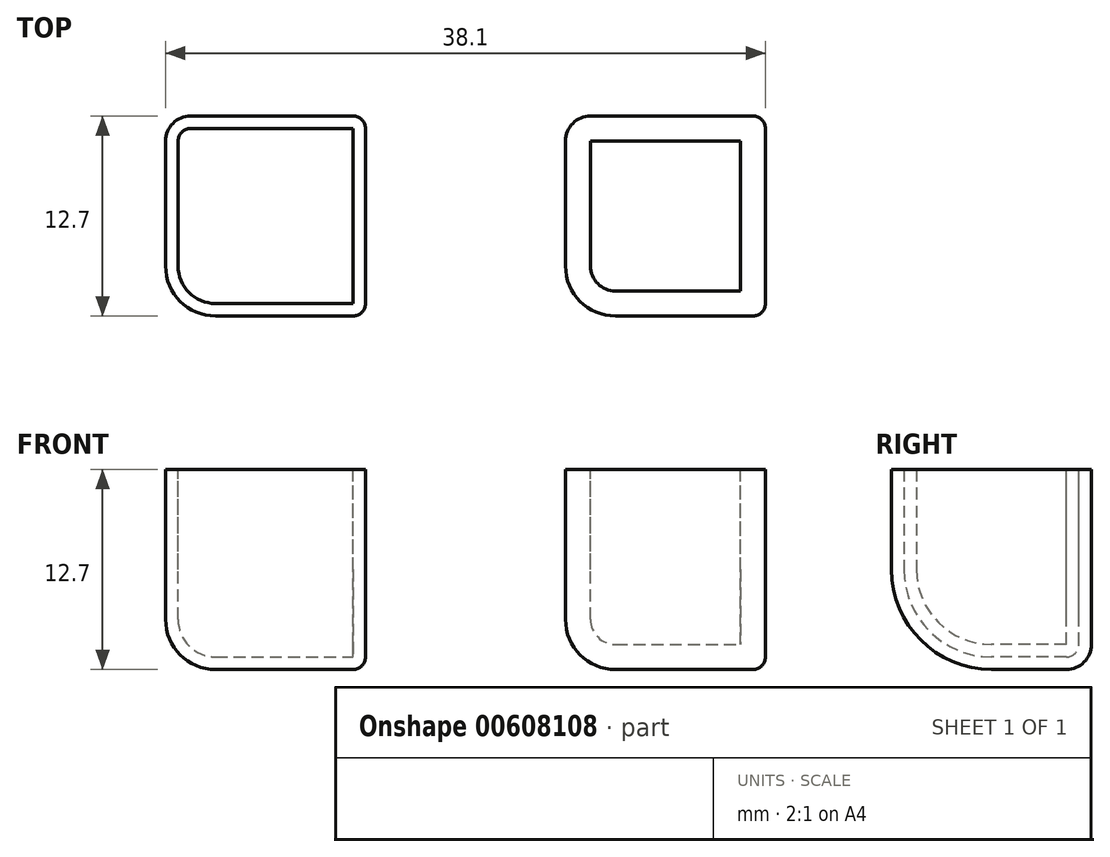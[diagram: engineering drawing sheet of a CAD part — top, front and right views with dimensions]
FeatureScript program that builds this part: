
annotation { "Feature Type Name" : "Feature", "Feature Type Description" : "" }
export const myFeature = defineFeature(function(context is Context, id is Id, definition is map)
    precondition{}
    {
        {
            var Q0;
            Q0=qCreatedBy(makeId("Top.planeOp"),FACE);
            var sketch = newSketch(context, id + "F0", { "sketchPlane" : qUnion([Q0])});
            skCircle(sketch, "E0.cCircle", {"center": v(0, 0) * mm, "radius": 6.35 * mm, "construction": true});
            skLineSegment(sketch, "E0.0", {"start": v(-6.35, 6.35) * mm, "end": v(6.35, 6.35) * mm});
            skLineSegment(sketch, "E0.1", {"start": v(6.35, 6.35) * mm, "end": v(6.35, -6.35) * mm});
            skLineSegment(sketch, "E0.2", {"start": v(6.35, -6.35) * mm, "end": v(-6.35, -6.35) * mm});
            skLineSegment(sketch, "E0.3", {"start": v(-6.35, -6.35) * mm, "end": v(-6.35, 6.35) * mm});
            skPoint(sketch, "E0.0.midPoint", {"position": v(0, 6.35) * mm});
            skSolve(sketch);
        }
        {
            var Q0;
            Q0=makeQuery(id+"F0.imprint","IMPRINT",FACE,{"disambiguationData":[TD([[makeQuery(id+"F0.imprint","IMPRINT",EDGE,{"derivedFrom":sQuery(id+"F0.wireOp",EDGE,"E0.0")}),-1.0]])]});
            extrude(context, id + "F1", {"entities" : qUnion([Q0]), "depth" : 12.7 * mm, "offsetDistance" : 25.4 * mm});
        }
        {
            var Q0;
            Q0=makeQuery(id+"F1.opExtrude","CAP_EDGE",EDGE,{"disambiguationData":[OSD([sQuery(id+"F0.wireOp",EDGE,"E0.2")])],"isStart":true});
            fillet(context, id + "F2", {"entities" : qUnion([Q0]), "radius" : 6.35 * mm, "tangentPropagation" : true, "allowEdgeOverflow" : false});
        }
        {
            var Q0;
            Q0=makeQuery(id+"F1.opExtrude","CAP_EDGE",EDGE,{"disambiguationData":[OSD([sQuery(id+"F0.wireOp",EDGE,"E0.3")])],"isStart":true});
            fillet(context, id + "F3", {"entities" : qUnion([Q0]), "radius" : 3.17 * mm, "tangentPropagation" : true, "allowEdgeOverflow" : false});
        }
        {
            var Q0;
            Q0=makeQuery(id+"F1.opExtrude","CAP_EDGE",EDGE,{"disambiguationData":[OSD([sQuery(id+"F0.wireOp",EDGE,"E0.0")])],"isStart":true});
            fillet(context, id + "F4", {"entities" : qUnion([Q0]), "radius" : 1.59 * mm, "tangentPropagation" : true, "allowEdgeOverflow" : false});
        }
        {
            var Q0;
            Q0=makeQuery(id+"F1.opExtrude","CAP_EDGE",EDGE,{"disambiguationData":[OSD([sQuery(id+"F0.wireOp",EDGE,"E0.1")])],"isStart":true});
            fillet(context, id + "F5", {"entities" : qUnion([Q0]), "radius" : 0.8 * mm, "tangentPropagation" : true, "allowEdgeOverflow" : false});
        }
        {
            var Q0;
            Q0=makeQuery(id+"F1.opExtrude","SWEPT_BODY",BODY,{"disambiguationData":[OSD([sQuery(id+"F0.wireOp",EDGE,"E0.0"),sQuery(id+"F0.wireOp",EDGE,"E0.1"),sQuery(id+"F0.wireOp",EDGE,"E0.2"),sQuery(id+"F0.wireOp",EDGE,"E0.3")])]});
            transform(context, id + "F6", {"entities" : qUnion([Q0]), "transformType" : TransformType.TRANSLATION_3D, "dx" : 25.4 * mm, "dy" : 0 * mm, "dz" : 0 * mm, "makeCopy" : true});
        }
        {
            var Q0;
            Q0=makeQuery(id+"F1.opExtrude","CAP_FACE",FACE,{"disambiguationData":[OSD([sQuery(id+"F0.wireOp",EDGE,"E0.0"),sQuery(id+"F0.wireOp",EDGE,"E0.1"),sQuery(id+"F0.wireOp",EDGE,"E0.2"),sQuery(id+"F0.wireOp",EDGE,"E0.3")])],"isStart":false});
            shell(context, id + "F7", {"entities" : qUnion([Q0]), "thickness" : 0.8 * mm});
        }
        {
            var Q0;
            Q0=makeQuery(id+"F6.opPattern","COPY",FACE,{"derivedFrom":makeQuery(id+"F1.opExtrude","CAP_FACE",FACE,{"disambiguationData":[OSD([sQuery(id+"F0.wireOp",EDGE,"E0.0"),sQuery(id+"F0.wireOp",EDGE,"E0.1"),sQuery(id+"F0.wireOp",EDGE,"E0.2"),sQuery(id+"F0.wireOp",EDGE,"E0.3")])],"isStart":false}),"instanceName":"1"});
            shell(context, id + "F8", {"entities" : qUnion([Q0]), "thickness" : 1.59 * mm});
        }
    });
